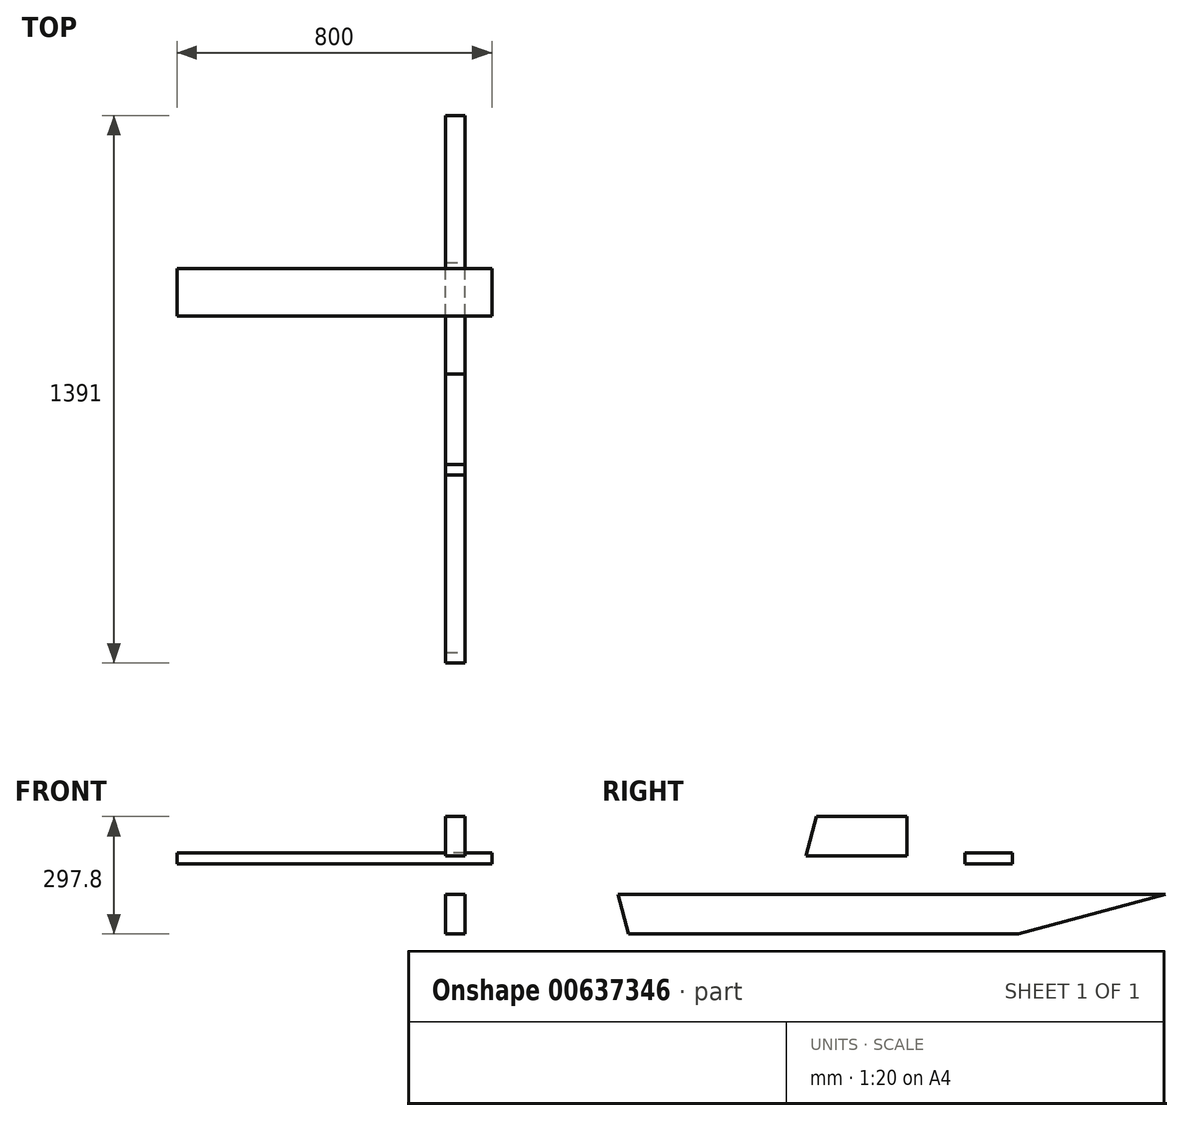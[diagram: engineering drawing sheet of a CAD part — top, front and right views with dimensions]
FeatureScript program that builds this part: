
annotation { "Feature Type Name" : "Feature", "Feature Type Description" : "" }
export const myFeature = defineFeature(function(context is Context, id is Id, definition is map)
    precondition{}
    {
        {
            var Q0;
            Q0=qCreatedBy(makeId("Right.planeOp"),FACE);
            var sketch = newSketch(context, id + "F0", { "sketchPlane" : qUnion([Q0])});
            skLineSegment(sketch, "E0.bottom", {"start": v(-643.77, -77.85) * mm, "end": v(747.23, -77.85) * mm});
            skLineSegment(sketch, "E0.top", {"start": v(-643.77, -177.85) * mm, "end": v(747.23, -177.85) * mm});
            skLineSegment(sketch, "E0.left", {"start": v(-643.77, -77.85) * mm, "end": v(-643.77, -177.85) * mm});
            skLineSegment(sketch, "E0.right", {"start": v(747.23, -77.85) * mm, "end": v(747.23, -177.85) * mm});
            skSolve(sketch);
        }
        {
            var Q0;
            Q0=makeQuery(id+"F0.imprint","IMPRINT",FACE,{"disambiguationData":[TD([[makeQuery(id+"F0.imprint","IMPRINT",EDGE,{"derivedFrom":sQuery(id+"F0.wireOp",EDGE,"E0.bottom")}),-1.0]])]});
            extrude(context, id + "F1", {"entities" : qUnion([Q0]), "depth" : 50 * mm, "offsetDistance" : 25 * mm});
        }
        {
            var Q0;
            Q0=makeQuery(id+"F1.opExtrude","CAP_FACE",FACE,{"disambiguationData":[OSD([sQuery(id+"F0.wireOp",EDGE,"E0.bottom"),sQuery(id+"F0.wireOp",EDGE,"E0.top"),sQuery(id+"F0.wireOp",EDGE,"E0.left"),sQuery(id+"F0.wireOp",EDGE,"E0.right")])],"isStart":false});
            var sketch = newSketch(context, id + "F2", { "sketchPlane" : qUnion([Q0])});
            skLineSegment(sketch, "E1", {"start": v(-643.77, -77.85) * mm, "end": v(-616.97, -177.85) * mm});
            skSolve(sketch);
        }
        {
            var Q0;
            {var subQ0=sQuery(id+"F2.wireOp",EDGE,"E1");Q0=makeQuery(id+"F2.imprint","IMPRINT",FACE,{"disambiguationData":[TD([[makeQuery(id+"F2.imprint","IMPRINT",EDGE,{"derivedFrom":subQ0}),-1.0]])]});}
            extrude(context, id + "F3", {"entities" : qUnion([Q0]), "operationType" : NewBodyOperationType.REMOVE, "endBound" : BoundingType.THROUGH_ALL, "oppositeDirection" : true, "depth" : 25 * mm, "offsetDistance" : 25 * mm});
        }
        {
            var Q0;
            Q0=makeQuery(id+"F1.opExtrude","CAP_FACE",FACE,{"disambiguationData":[OSD([sQuery(id+"F0.wireOp",EDGE,"E0.bottom"),sQuery(id+"F0.wireOp",EDGE,"E0.top"),sQuery(id+"F0.wireOp",EDGE,"E0.left"),sQuery(id+"F0.wireOp",EDGE,"E0.right")])],"isStart":false});
            var sketch = newSketch(context, id + "F4", { "sketchPlane" : qUnion([Q0])});
            skLineSegment(sketch, "E2", {"start": v(747.23, -77.85) * mm, "end": v(374.03, -177.85) * mm});
            skSolve(sketch);
        }
        {
            var Q0;
            {var subQ0=sQuery(id+"F4.wireOp",EDGE,"E2");Q0=makeQuery(id+"F4.imprint","IMPRINT",FACE,{"disambiguationData":[TD([[makeQuery(id+"F4.imprint","IMPRINT",EDGE,{"derivedFrom":subQ0}),1.0]])]});}
            extrude(context, id + "F5", {"entities" : qUnion([Q0]), "operationType" : NewBodyOperationType.REMOVE, "endBound" : BoundingType.THROUGH_ALL, "oppositeDirection" : true, "depth" : 25 * mm, "offsetDistance" : 25 * mm});
        }
        {
            var Q0;
            Q0=qCreatedBy(makeId("Right.planeOp"),FACE);
            var sketch = newSketch(context, id + "F6", { "sketchPlane" : qUnion([Q0])});
            skLineSegment(sketch, "E3.bottom", {"start": v(-165.88, 19.95) * mm, "end": v(91.12, 19.95) * mm});
            skLineSegment(sketch, "E3.top", {"start": v(-165.88, 119.95) * mm, "end": v(91.12, 119.95) * mm});
            skLineSegment(sketch, "E3.left", {"start": v(-165.88, 19.95) * mm, "end": v(-165.88, 119.95) * mm});
            skLineSegment(sketch, "E3.right", {"start": v(91.12, 19.95) * mm, "end": v(91.12, 119.95) * mm});
            skSolve(sketch);
        }
        {
            var Q0;
            Q0=makeQuery(id+"F6.imprint","IMPRINT",FACE,{"disambiguationData":[TD([[makeQuery(id+"F6.imprint","IMPRINT",EDGE,{"derivedFrom":sQuery(id+"F6.wireOp",EDGE,"E3.bottom")}),1.0]])]});
            extrude(context, id + "F7", {"entities" : qUnion([Q0]), "depth" : 50 * mm, "offsetDistance" : 25 * mm});
        }
        {
            var Q0;
            Q0=makeQuery(id+"F7.opExtrude","CAP_FACE",FACE,{"disambiguationData":[OSD([sQuery(id+"F6.wireOp",EDGE,"E3.bottom"),sQuery(id+"F6.wireOp",EDGE,"E3.top"),sQuery(id+"F6.wireOp",EDGE,"E3.left"),sQuery(id+"F6.wireOp",EDGE,"E3.right")])],"isStart":false});
            var sketch = newSketch(context, id + "F8", { "sketchPlane" : qUnion([Q0])});
            skLineSegment(sketch, "E4", {"start": v(-165.88, 19.95) * mm, "end": v(-139.08, 119.95) * mm});
            skSolve(sketch);
        }
        {
            var Q0;
            {var subQ0=sQuery(id+"F8.wireOp",EDGE,"E4");Q0=makeQuery(id+"F8.imprint","IMPRINT",FACE,{"disambiguationData":[TD([[makeQuery(id+"F8.imprint","IMPRINT",EDGE,{"derivedFrom":subQ0}),1.0]])]});}
            extrude(context, id + "F9", {"entities" : qUnion([Q0]), "operationType" : NewBodyOperationType.REMOVE, "endBound" : BoundingType.THROUGH_ALL, "oppositeDirection" : true, "depth" : 25 * mm, "offsetDistance" : 25 * mm});
        }
        {
            var Q0;
            Q0=qCreatedBy(makeId("Top.planeOp"),FACE);
            var sketch = newSketch(context, id + "F10", { "sketchPlane" : qUnion([Q0])});
            skLineSegment(sketch, "E5.bottom", {"start": v(117.55, 238.74) * mm, "end": v(-682.45, 238.74) * mm});
            skLineSegment(sketch, "E5.top", {"start": v(117.55, 358.74) * mm, "end": v(-682.45, 358.74) * mm});
            skLineSegment(sketch, "E5.left", {"start": v(117.55, 238.74) * mm, "end": v(117.55, 358.74) * mm});
            skLineSegment(sketch, "E5.right", {"start": v(-682.45, 238.74) * mm, "end": v(-682.45, 358.74) * mm});
            skSolve(sketch);
        }
        {
            var Q0;
            Q0=makeQuery(id+"F10.imprint","IMPRINT",FACE,{"disambiguationData":[TD([[makeQuery(id+"F10.imprint","IMPRINT",EDGE,{"derivedFrom":sQuery(id+"F10.wireOp",EDGE,"E5.bottom")}),-1.0]])]});
            extrude(context, id + "F11", {"entities" : qUnion([Q0]), "depth" : 28 * mm, "offsetDistance" : 25 * mm});
        }
    });
